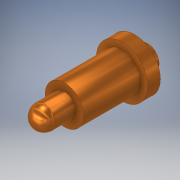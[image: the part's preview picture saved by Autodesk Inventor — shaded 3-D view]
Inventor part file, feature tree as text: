
AUTODESK INVENTOR PART (.ipt)
format: ipt  version: 2019 (Build 230136000, 136)  size: 131,584 bytes
history: native  units: mm
features: extrude x4, sketch x4, fillet x1
ambient origin geometry x8: Origin, YZ Plane, XZ Plane, XY Plane, X Axis, Y Axis, Z Axis, Center Point
bodies: Volumenkörper1 (feature_tree)
feature tree (9):
  extrude  "Extrusion1"  Depth=0.5mm TaperAngle=0.0deg
  extrude  "Extrusion2"  Depth=2.25mm TaperAngle=0.0deg
  extrude  "Extrusion3"  Depth=0.45mm TaperAngle=0.0deg
  fillet  "Rundung1"  Radius=0.45mm
  extrude  "Extrusion4"  Depth=0.5mm TaperAngle=0.0deg
  sketch  "Skizze1"  dims[d0=2.0mm d1=0.5mm d2=0.0mm]
  sketch  "Skizze2"  dims[d3=1.5mm d4=2.25mm d5=0.0mm]
  sketch  "Skizze3"  dims[d6=0.9mm d7=1.25mm d8=0.0mm d9=0.45mm]
  sketch  "Skizze4"  dims[d10=0.9mm d11=0.5mm d12=0.0mm]
